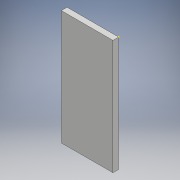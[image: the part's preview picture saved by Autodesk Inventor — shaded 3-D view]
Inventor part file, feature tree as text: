
AUTODESK INVENTOR PART (.ipt)
format: ipt  version: 2017 SP1 (Build 210196100, 196)  size: 90,624 bytes
history: native  units: mm
features: sketch x2, extrude x1
ambient origin geometry x8: Origin, YZ Plane, XZ Plane, XY Plane, X Axis, Y Axis, Z Axis, Center Point
bodies: Solide1 (feature_tree)
feature tree (3):
  extrude  "Extrusion1"  Depth=90.0mm
  sketch  "Esquisse2"
  sketch  "Esquisse1"
